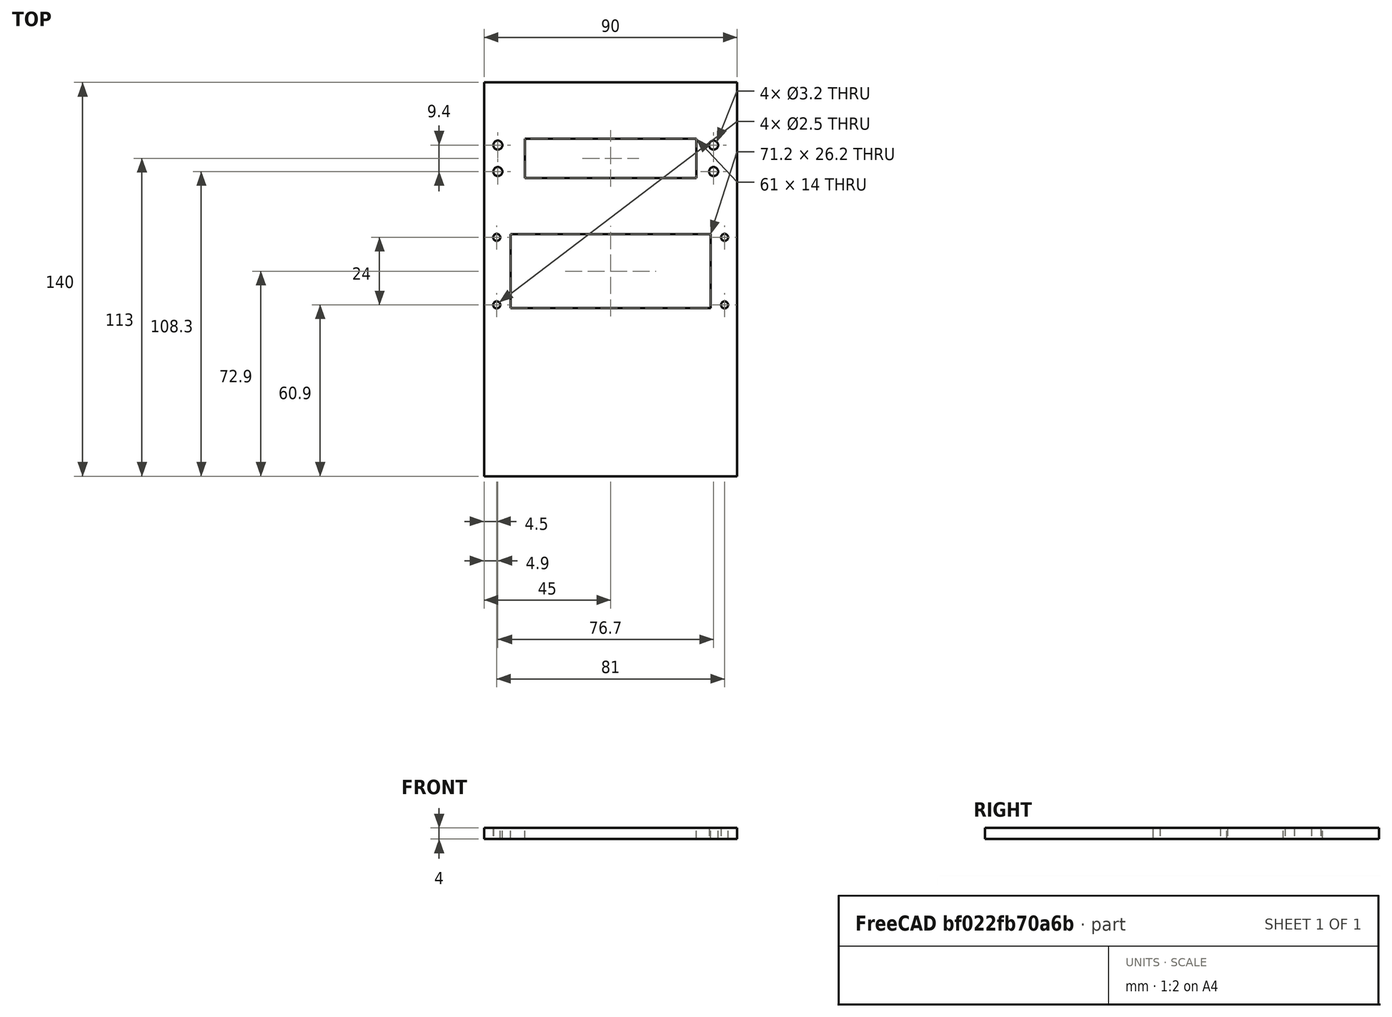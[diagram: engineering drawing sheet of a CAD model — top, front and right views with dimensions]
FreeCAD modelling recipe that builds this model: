
FCSTD DOCUMENT  (FreeCAD 0.20R29603 (Git))
Label: baseplate
License: All rights reserved
LicenseURL: http://en.wikipedia.org/wiki/All_rights_reserved
objects: TechDraw::DrawViewDimension×12, Sketcher::SketchObject×1, TechDraw::DrawSVGTemplate×1, TechDraw::DrawViewPart×1, PartDesign::Pad×1, PartDesign::Body×1, TechDraw::DrawProjGroupItem×1, TechDraw::DrawProjGroup×1, TechDraw::DrawPage×1
note: 4 computed .brp shape members not serialized (recipe doc carries the construction recipe); baked Part::Feature solids carry a one-line shape summary decoded from their .brp

FEATURE [Sketcher::SketchObject] Sketch
  FullyConstrained = true
  MapMode = 5
  Support = -> [XY_Plane]
  sketch-geometry (20):
    g0: LineSegment StartX=-45 StartY=-70 StartZ=0 EndX=45 EndY=-70 EndZ=0
    g1: LineSegment StartX=45 StartY=-70 StartZ=0 EndX=45 EndY=70 EndZ=0
    g2: LineSegment StartX=45 StartY=70 StartZ=0 EndX=-45 EndY=70 EndZ=0
    g3: LineSegment StartX=-45 StartY=70 StartZ=0 EndX=-45 EndY=-70 EndZ=0
    g4: LineSegment StartX=-35.6 StartY=16 StartZ=0 EndX=35.6 EndY=16 EndZ=0
    g5: LineSegment StartX=35.6 StartY=16 StartZ=0 EndX=35.6 EndY=-10.2 EndZ=0
    g6: LineSegment StartX=35.6 StartY=-10.2 StartZ=0 EndX=-35.6 EndY=-10.2 EndZ=0
    g7: LineSegment StartX=-35.6 StartY=-10.2 StartZ=0 EndX=-35.6 EndY=16 EndZ=0
    g8: Circle CenterX=-40.5 CenterY=14.9 CenterZ=0 NormalX=0 NormalY=0 NormalZ=1 AngleXU=0 Radius=1.25
    g9: Circle CenterX=-40.5 CenterY=-9.1 CenterZ=0 NormalX=0 NormalY=0 NormalZ=1 AngleXU=0 Radius=1.25
    g10: Circle CenterX=40.5 CenterY=14.9 CenterZ=0 NormalX=0 NormalY=0 NormalZ=1 AngleXU=0 Radius=1.25
    g11: Circle CenterX=40.5 CenterY=-9.1 CenterZ=0 NormalX=0 NormalY=0 NormalZ=1 AngleXU=0 Radius=1.25
    g12: LineSegment StartX=-30.5 StartY=50 StartZ=0 EndX=30.5 EndY=50 EndZ=0
    g13: LineSegment StartX=30.5 StartY=50 StartZ=0 EndX=30.5 EndY=36 EndZ=0
    g14: LineSegment StartX=30.5 StartY=36 StartZ=0 EndX=-30.5 EndY=36 EndZ=0
    g15: LineSegment StartX=-30.5 StartY=36 StartZ=0 EndX=-30.5 EndY=50 EndZ=0
    g16: Circle CenterX=-40.1 CenterY=47.7 CenterZ=0 NormalX=0 NormalY=0 NormalZ=1 AngleXU=0 Radius=1.6
    g17: Circle CenterX=-40.1 CenterY=38.3 CenterZ=0 NormalX=0 NormalY=0 NormalZ=1 AngleXU=0 Radius=1.6
    g18: Circle CenterX=36.6 CenterY=47.7 CenterZ=0 NormalX=0 NormalY=0 NormalZ=1 AngleXU=0 Radius=1.6
    g19: Circle CenterX=36.6 CenterY=38.3 CenterZ=0 NormalX=0 NormalY=0 NormalZ=1 AngleXU=0 Radius=1.6
  constraints (57):
    c: Coincident(g0,g1)
    c: Coincident(g1,g2)
    c: Coincident(g2,g3)
    c: Coincident(g3,g0)
    c: Horizontal(g0)
    c: Horizontal(g2)
    c: Vertical(g1)
    c: Vertical(g3)
    c: DistanceX(g2,g2) = 90
    c: DistanceY(g1,g1) = 140
    c: Symmetric(g2,g0,g-1)
    c: Coincident(g4,g5)
    c: Coincident(g5,g6)
    c: Coincident(g6,g7)
    c: Coincident(g7,g4)
    c: Horizontal(g6)
    c: Vertical(g5)
    c: Vertical(g7)
    c: DistanceX(g4,g4) = 71.2
    c: DistanceY(g5,g5) = 26.2
    c: Symmetric(g4,g4,g-2)
    c: Diameter(g8) = 2.5
    c: DistanceX(g8,g4) = 4.9
    c: DistanceY(g4,g8) = -1.1
    c: Diameter(g9) = 2.5
    c: DistanceX(g9,g6) = 4.9
    c: DistanceY(g9,g6) = -1.1
    c: Diameter(g10) = 2.5
    c: Diameter(g11) = 2.5
    c: DistanceX(g4,g10) = 4.9
    c: DistanceY(g4,g10) = -1.1
    c: DistanceX(g5,g11) = 4.9
    c: DistanceY(g11,g5) = -1.1
    c: Coincident(g12,g13)
    c: Coincident(g13,g14)
    c: Coincident(g14,g15)
    c: Coincident(g15,g12)
    c: Horizontal(g14)
    c: Vertical(g13)
    c: Vertical(g15)
    c: DistanceX(g12,g12) = 61
    c: DistanceY(g15,g15) = 14
    c: Symmetric(g12,g12,g-2)
    c: Diameter(g16) = 3.2
    c: Diameter(g18) = 3.2
    c: Diameter(g17) = 3.2
    c: Diameter(g19) = 3.2
    c: DistanceX(g16,g12) = 9.6
    c: DistanceX(g17,g14) = 9.6
    c: DistanceX(g12,g18) = 6.1
    c: DistanceX(g13,g19) = 6.1
    c: DistanceY(g18,g12) = 2.3
    c: DistanceY(g13,g19) = 2.3
    c: DistanceY(g14,g17) = 2.3
    c: DistanceY(g16,g12) = 2.3
    c: DistanceY(g12,g2) = 20
    c: DistanceY(g4,g14) = 20
FEATURE [TechDraw::DrawSVGTemplate] Template
  EditableTexts = AUTHOR_NAME=AUTHOR NAME; DN=DN; DRAWING_TITLE=DRAWING TITLE; FC-DATE=DD/MM/YYYY; FC-REV=REV A; FC-SC=SCALE; FC-SH=X / Y; FC-SI=A4; FreeCAD_DRAWING=FreeCAD DRAWING; PN=PN
  Height = 297
  Orientation = 0
  Width = 210
FEATURE [TechDraw::DrawViewPart] View
  CoarseView = false
  Direction = (0,0,1)
  Focus = 100
  HardHidden = false
  IsoCount = 0
  IsoHidden = false
  IsoVisible = false
  LockPosition = false
  Perspective = false
  Rotation = 0
  ScaleType = 0
  SeamHidden = false
  SeamVisible = true
  SmoothHidden = false
  SmoothVisible = true
  Source = -> [Template]
  X = 105
  XDirection = (1,0,0)
  Y = 148.5
FEATURE [PartDesign::Pad] Pad
  Direction = (0,0,1)
  Length = 4
  Length2 = 10
  Profile = -> Sketch
  ReferenceAxis = -> Sketch [N_Axis]
  Type = 0
FEATURE [PartDesign::Body] Body
  Group = -> [Sketch,Pad]
  Origin = -> Origin
  Tip = -> Pad
FEATURE [TechDraw::DrawProjGroupItem] ProjItem  label="Front"
  CoarseView = false
  Direction = (0,0,1)
  Focus = 100
  HardHidden = false
  IsoCount = 0
  IsoHidden = false
  IsoVisible = false
  LockPosition = true
  Perspective = false
  Rotation = 0
  RotationVector = (1,0,0)
  ScaleType = 2
  SeamHidden = false
  SeamVisible = true
  SmoothHidden = false
  SmoothVisible = true
  Source = -> [Pad]
  Type = 0
  X = 0
  XDirection = (1,0,0)
  Y = 0
FEATURE [TechDraw::DrawProjGroup] ProjGroup
  Anchor = -> ProjItem
  AutoDistribute = true
  LockPosition = false
  ProjectionType = 0
  Rotation = 0
  ScaleType = 0
  Source = -> [Pad]
  Views = -> [ProjItem]
  X = 105
  Y = 148.5
  spacingX = 15
  spacingY = 15
FEATURE [TechDraw::DrawViewDimension] Dimension
  AngleOverride = false
  Arbitrary = false
  ArbitraryTolerances = false
  EqualTolerance = true
  ExtensionAngle = 0
  FormatSpec = %.2w
  FormatSpecOverTolerance = %+.2w
  FormatSpecUnderTolerance = %+.2w
  Inverted = false
  LineAngle = 0
  LockPosition = false
  MeasureType = 1
  OverTolerance = 0
  References2D = -> [ProjItem]
  Rotation = 0
  ScaleType = 0
  TheoreticalExact = false
  Type = 1
  UnderTolerance = 0
  X = -0.138179
  Y = 105.666
FEATURE [TechDraw::DrawViewDimension] Dimension001
  AngleOverride = false
  Arbitrary = false
  ArbitraryTolerances = false
  EqualTolerance = true
  ExtensionAngle = 0
  FormatSpec = %.2w
  FormatSpecOverTolerance = %+.2w
  FormatSpecUnderTolerance = %+.2w
  Inverted = false
  LineAngle = 0
  LockPosition = false
  MeasureType = 1
  OverTolerance = 0
  References2D = -> [ProjItem]
  Rotation = 0
  ScaleType = 0
  TheoreticalExact = false
  Type = 2
  UnderTolerance = 0
  X = -66.9077
  Y = 60.1405
FEATURE [TechDraw::DrawViewDimension] Dimension002
  AngleOverride = false
  Arbitrary = false
  ArbitraryTolerances = false
  EqualTolerance = true
  ExtensionAngle = 0
  FormatSpec = %.2w
  FormatSpecOverTolerance = %+.2w
  FormatSpecUnderTolerance = %+.2w
  Inverted = false
  LineAngle = 0
  LockPosition = false
  MeasureType = 1
  OverTolerance = 0
  References2D = -> [ProjItem]
  Rotation = 0
  ScaleType = 0
  TheoreticalExact = false
  Type = 2
  UnderTolerance = 0
  X = -74.1804
  Y = 43.6857
FEATURE [TechDraw::DrawViewDimension] Dimension003
  AngleOverride = false
  Arbitrary = false
  ArbitraryTolerances = false
  EqualTolerance = true
  ExtensionAngle = 0
  FormatSpec = %.2w
  FormatSpecOverTolerance = %+.2w
  FormatSpecUnderTolerance = %+.2w
  Inverted = false
  LineAngle = 0
  LockPosition = false
  MeasureType = 1
  OverTolerance = 0
  References2D = -> [ProjItem]
  Rotation = 0
  ScaleType = 0
  TheoreticalExact = false
  Type = 2
  UnderTolerance = 0
  X = -81.4339
  Y = 28.109
FEATURE [TechDraw::DrawViewDimension] Dimension009
  AngleOverride = false
  Arbitrary = false
  ArbitraryTolerances = false
  EqualTolerance = true
  ExtensionAngle = 0
  FormatSpec = %.2w
  FormatSpecOverTolerance = %+.2w
  FormatSpecUnderTolerance = %+.2w
  Inverted = false
  LineAngle = 0
  LockPosition = false
  MeasureType = 1
  OverTolerance = 0
  References2D = -> [ProjItem]
  Rotation = 0
  ScaleType = 0
  TheoreticalExact = false
  Type = 1
  UnderTolerance = 0
  X = -56.5055
  Y = -52.8841
FEATURE [TechDraw::DrawViewDimension] Dimension010
  AngleOverride = false
  Arbitrary = false
  ArbitraryTolerances = false
  EqualTolerance = true
  ExtensionAngle = 0
  FormatSpec = %.2w
  FormatSpecOverTolerance = %+.2w
  FormatSpecUnderTolerance = %+.2w
  Inverted = false
  LineAngle = 0
  LockPosition = false
  MeasureType = 1
  OverTolerance = 0
  References2D = -> [ProjItem]
  Rotation = 0
  ScaleType = 0
  TheoreticalExact = false
  Type = 1
  UnderTolerance = 0
  X = 1.20951
  Y = -44.2542
FEATURE [TechDraw::DrawViewDimension] Dimension011
  AngleOverride = false
  Arbitrary = false
  ArbitraryTolerances = false
  EqualTolerance = true
  ExtensionAngle = 0
  FormatSpec = %.2w
  FormatSpecOverTolerance = %+.2w
  FormatSpecUnderTolerance = %+.2w
  Inverted = false
  LineAngle = 0
  LockPosition = false
  MeasureType = 1
  OverTolerance = 0
  References2D = -> [ProjItem]
  Rotation = 0
  ScaleType = 0
  TheoreticalExact = false
  Type = 1
  UnderTolerance = 0
  X = -56.1675
  Y = 87.9927
FEATURE [TechDraw::DrawViewDimension] Dimension012
  AngleOverride = false
  Arbitrary = false
  ArbitraryTolerances = false
  EqualTolerance = true
  ExtensionAngle = 0
  FormatSpec = %.2w
  FormatSpecOverTolerance = %+.2w
  FormatSpecUnderTolerance = %+.2w
  Inverted = false
  LineAngle = 0
  LockPosition = false
  MeasureType = 1
  OverTolerance = 0
  References2D = -> [ProjItem]
  Rotation = 0
  ScaleType = 0
  TheoreticalExact = false
  Type = 1
  UnderTolerance = 0
  X = 4.13865
  Y = 95.9407
FEATURE [TechDraw::DrawViewDimension] Dimension013
  AngleOverride = false
  Arbitrary = false
  ArbitraryTolerances = false
  EqualTolerance = true
  ExtensionAngle = 0
  FormatSpec = ⌀%.2w
  FormatSpecOverTolerance = %+.2w
  FormatSpecUnderTolerance = %+.2w
  Inverted = false
  LineAngle = 0
  LockPosition = false
  MeasureType = 1
  OverTolerance = 0
  References2D = -> [ProjItem]
  Rotation = 0
  ScaleType = 0
  TheoreticalExact = false
  Type = 5
  UnderTolerance = 0
  X = 24.8427
  Y = 30.7314
FEATURE [TechDraw::DrawViewDimension] Dimension014
  AngleOverride = false
  Arbitrary = false
  ArbitraryTolerances = false
  EqualTolerance = true
  ExtensionAngle = 0
  FormatSpec = ⌀%.2w
  FormatSpecOverTolerance = %+.2w
  FormatSpecUnderTolerance = %+.2w
  Inverted = false
  LineAngle = 0
  LockPosition = false
  MeasureType = 1
  OverTolerance = 0
  References2D = -> [ProjItem]
  Rotation = 0
  ScaleType = 0
  TheoreticalExact = false
  Type = 5
  UnderTolerance = 0
  X = 49.5015
  Y = 30.3634
FEATURE [TechDraw::DrawViewDimension] Dimension015
  AngleOverride = false
  Arbitrary = false
  ArbitraryTolerances = false
  EqualTolerance = true
  ExtensionAngle = 0
  FormatSpec = %.2w
  FormatSpecOverTolerance = %+.2w
  FormatSpecUnderTolerance = %+.2w
  Inverted = false
  LineAngle = 0
  LockPosition = false
  MeasureType = 1
  OverTolerance = 0
  References2D = -> [ProjItem]
  Rotation = 0
  ScaleType = 0
  TheoreticalExact = false
  Type = 2
  UnderTolerance = 0
  X = 66.5462
  Y = 1.65505
FEATURE [TechDraw::DrawViewDimension] Dimension016
  AngleOverride = false
  Arbitrary = false
  ArbitraryTolerances = false
  EqualTolerance = true
  ExtensionAngle = 0
  FormatSpec = %.2w
  FormatSpecOverTolerance = %+.2w
  FormatSpecUnderTolerance = %+.2w
  Inverted = false
  LineAngle = 0
  LockPosition = false
  MeasureType = 1
  OverTolerance = 0
  References2D = -> [ProjItem]
  Rotation = 0
  ScaleType = 0
  TheoreticalExact = false
  Type = 2
  UnderTolerance = 0
  X = -73.7638
  Y = 4.93337
FEATURE [TechDraw::DrawPage] Page
  KeepUpdated = true
  NextBalloonIndex = 1
  ProjectionType = 0
  Template = -> Template
  Views = -> [View,ProjGroup,Dimension,Dimension001,Dimension002,Dimension003,Dimension009,Dimension010,Dimension011,Dimension012,Dimension013,Dimension014,Dimension015,Dimension016]
